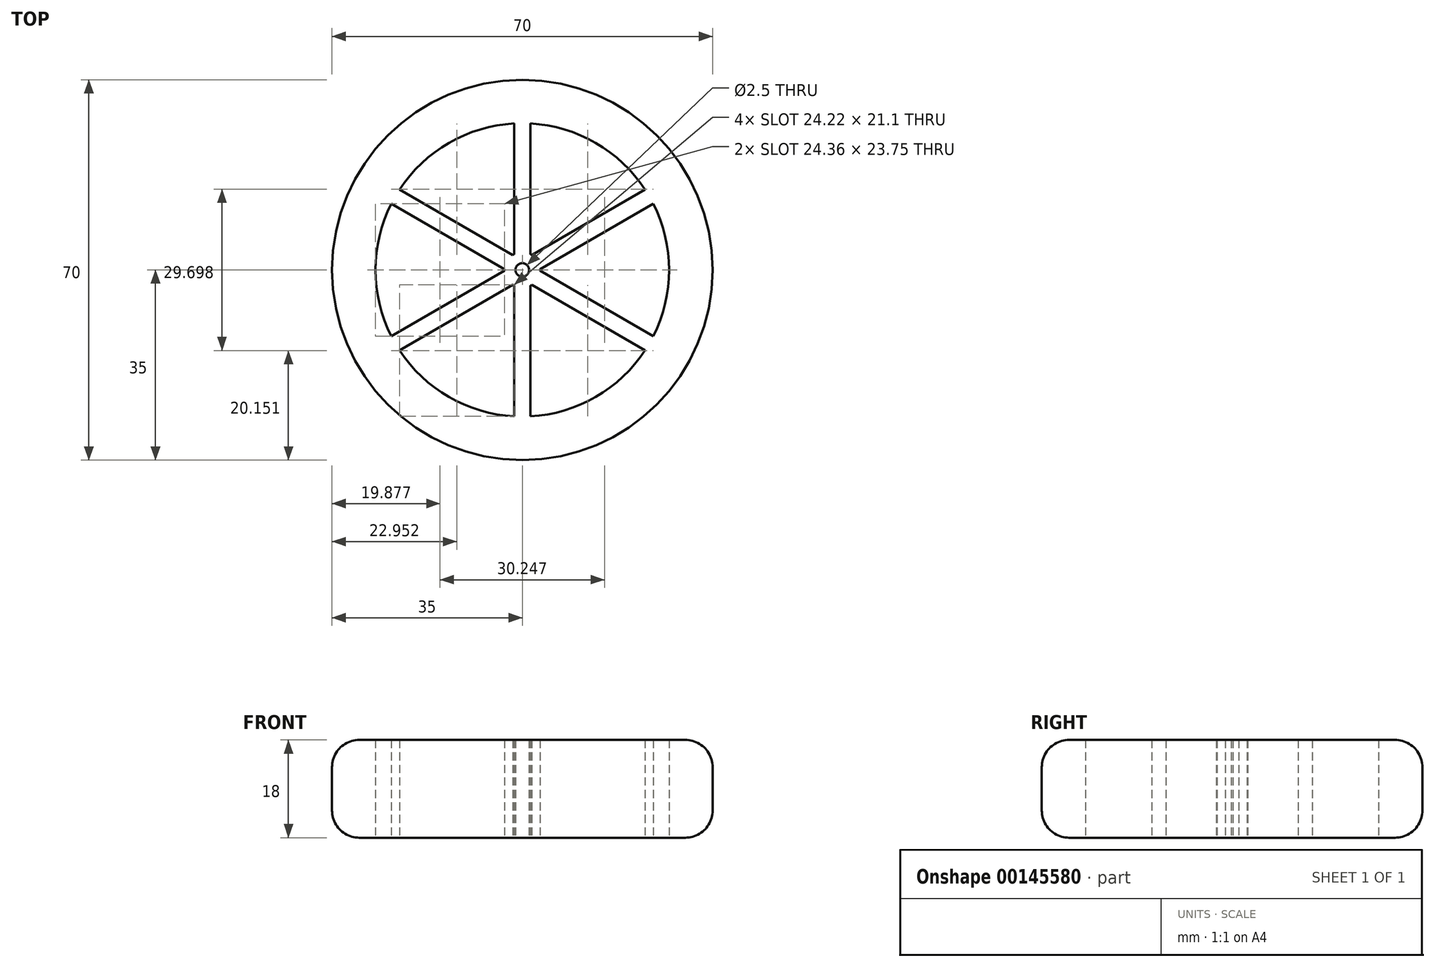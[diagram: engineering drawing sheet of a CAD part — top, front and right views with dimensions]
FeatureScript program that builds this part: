
annotation { "Feature Type Name" : "Feature", "Feature Type Description" : "" }
export const myFeature = defineFeature(function(context is Context, id is Id, definition is map)
    precondition{}
    {
        {
            var Q0;
            Q0=qCreatedBy(makeId("Top.planeOp"),FACE);
            var sketch = newSketch(context, id + "F0", { "sketchPlane" : qUnion([Q0])});
            skCircle(sketch, "E0", {"center": v(0, 0) * mm, "radius": 35 * mm});
            skCircle(sketch, "E1.0", {"center": v(0, 0) * mm, "radius": 27 * mm});
            skCircle(sketch, "E2", {"center": v(0, 0) * mm, "radius": 1.25 * mm});
            skCircle(sketch, "E3.0", {"center": v(0, 0) * mm, "radius": 3.25 * mm});
            skLineSegment(sketch, "E4", {"start": v(-1.5, 2.88) * mm, "end": v(-1.5, 26.96) * mm});
            skLineSegment(sketch, "E5.MirrorCS", {"start": v(1.5, 2.88) * mm, "end": v(1.5, 26.96) * mm});
            skLineSegment(sketch, "E6.1.0", {"start": v(-3.25, 0.14) * mm, "end": v(-24.1, 12.18) * mm});
            skLineSegment(sketch, "E6.1.1", {"start": v(-1.75, 2.74) * mm, "end": v(-22.6, 14.78) * mm});
            skLineSegment(sketch, "E6.2.0", {"start": v(-1.75, -2.74) * mm, "end": v(-22.6, -14.78) * mm});
            skLineSegment(sketch, "E6.2.1", {"start": v(-3.25, -0.14) * mm, "end": v(-24.1, -12.18) * mm});
            skLineSegment(sketch, "E6.3.0", {"start": v(1.5, -2.88) * mm, "end": v(1.5, -26.96) * mm});
            skLineSegment(sketch, "E6.3.1", {"start": v(-1.5, -2.88) * mm, "end": v(-1.5, -26.96) * mm});
            skLineSegment(sketch, "E6.4.0", {"start": v(3.25, -0.14) * mm, "end": v(24.1, -12.18) * mm});
            skLineSegment(sketch, "E6.4.1", {"start": v(1.75, -2.74) * mm, "end": v(22.6, -14.78) * mm});
            skLineSegment(sketch, "E6.5.0", {"start": v(1.75, 2.74) * mm, "end": v(22.6, 14.78) * mm});
            skLineSegment(sketch, "E6.5.1", {"start": v(3.25, 0.14) * mm, "end": v(24.1, 12.18) * mm});
            skSolve(sketch);
        }
        {
            var Q0;
            {var subQ0=sQuery(id+"F0.wireOp",EDGE,"E6.2.0");Q0=makeQuery(id+"F0.imprint","IMPRINT",FACE,{"disambiguationData":[TD([[makeQuery(id+"F0.imprint","IMPRINT",EDGE,{"derivedFrom":subQ0}),-1.0]])]});}
            var Q1;
            {var subQ0=sQuery(id+"F0.wireOp",EDGE,"E6.1.0");Q1=makeQuery(id+"F0.imprint","IMPRINT",FACE,{"disambiguationData":[TD([[makeQuery(id+"F0.imprint","IMPRINT",EDGE,{"derivedFrom":subQ0}),-1.0]])]});}
            var Q2;
            {var subQ0=sQuery(id+"F0.wireOp",EDGE,"E4");Q2=makeQuery(id+"F0.imprint","IMPRINT",FACE,{"disambiguationData":[TD([[makeQuery(id+"F0.imprint","IMPRINT",EDGE,{"derivedFrom":subQ0}),-1.0]])]});}
            var Q3;
            {var subQ0=sQuery(id+"F0.wireOp",EDGE,"E6.5.0");Q3=makeQuery(id+"F0.imprint","IMPRINT",FACE,{"disambiguationData":[TD([[makeQuery(id+"F0.imprint","IMPRINT",EDGE,{"derivedFrom":subQ0}),-1.0]])]});}
            var Q4;
            {var subQ0=sQuery(id+"F0.wireOp",EDGE,"E6.4.0");Q4=makeQuery(id+"F0.imprint","IMPRINT",FACE,{"disambiguationData":[TD([[makeQuery(id+"F0.imprint","IMPRINT",EDGE,{"derivedFrom":subQ0}),-1.0]])]});}
            var Q5;
            {var subQ0=sQuery(id+"F0.wireOp",EDGE,"E6.3.0");Q5=makeQuery(id+"F0.imprint","IMPRINT",FACE,{"disambiguationData":[TD([[makeQuery(id+"F0.imprint","IMPRINT",EDGE,{"derivedFrom":subQ0}),-1.0]])]});}
            var Q6;
            Q6=makeQuery(id+"F0.imprint","IMPRINT",FACE,{"disambiguationData":[TD([[makeQuery(id+"F0.imprint","IMPRINT",EDGE,{"derivedFrom":sQuery(id+"F0.wireOp",EDGE,"E2")}),-1.0]])]});
            var Q7;
            Q7=makeQuery(id+"F0.imprint","IMPRINT",FACE,{"disambiguationData":[TD([[makeQuery(id+"F0.imprint","IMPRINT",EDGE,{"derivedFrom":sQuery(id+"F0.wireOp",EDGE,"E0")}),1.0]])]});
            extrude(context, id + "F1", {"entities" : qUnion([Q0, Q1, Q2, Q3, Q4, Q5, Q6, Q7]), "depth" : 18 * mm});
        }
        {
            var Q0;
            Q0=makeQuery(id+"F1.opExtrude","CAP_EDGE",EDGE,{"disambiguationData":[OSD([sQuery(id+"F0.wireOp",EDGE,"E0")])],"isStart":false});
            var Q1;
            Q1=makeQuery(id+"F1.opExtrude","CAP_EDGE",EDGE,{"disambiguationData":[OSD([sQuery(id+"F0.wireOp",EDGE,"E0")])],"isStart":true});
            fillet(context, id + "F2", {"entities" : qUnion([Q0, Q1]), "radius" : 5 * mm, "tangentPropagation" : true, "allowEdgeOverflow" : false});
        }
    });
